# Revit family: Varmax_275_320_2-3Piquages - depuis 2013-12_FR_B
name_source: partatom
category: Equipement de génie climatique
revit_build: Autodesk Revit 2015 (Build: 20140606_1530(x64)
units: mm (PartAtom-declared; Revit-internal decimal feet)

## types (2) — shared parameters
Classe Nox = 6
Fabricant = Atlantic
Famille = Chaudière collective sol gaz
Fréquence = 50 Hz
Garantie autres pièces = 2 ans
Garantie corps de chauffe = 3 ans
Hauteur = 1877 mm  [stored 6.15814 ft]
Hauteur chaudière (hors pieds) = 1877 mm  [stored 6.15814 ft]
Hauteur de pieds mini = 45 mm
Hauteur entrée d’air (hors pieds) = 1256 mm
Hauteur piquage départ (hors pieds) = 1661 mm  [stored 5.44948 ft]
Hauteur piquage gaz (hors pieds) = 1413 mm
Hauteur piquage retour chaud (hors pieds) = 1265 mm
Largeur = 812 mm  [stored 2.66404 ft]
Largeur chaudière = 779 mm  [stored 2.55577 ft]
Largeur chaudière avec jaquette = 812 mm  [stored 2.66404 ft]
Lien données RT (Edibatec) = http://www.edibatec.org
Lien page produit = http://www.atlantic-guillot.fr
Lien pièces détachées = http://atlantic.plateforme-services.com
Longueur piquages départ / retour = 148 mm
Marque commerciale = Oui
Marque3D = Oui
Matériau corps de chauffe = Acier inoxydable
Modèle = Varmax 275
Nombre piquages = 3
Poids à vide = 502 kg
Pression d'alimentation gaz naturel = 20 ou 300 mbar
Pression d'alimentation propane = 37 mbar
Pression de service = 6 bar
Profondeur = 1341 mm  [stored 4.39961 ft]
Profondeur chaudière = 1341 mm  [stored 4.39961 ft]
Raccordement fumées = Cheminée (B23/B23p) / Ventouse (C13/C33/C53)
Réseau (mono/tri) = Monophasé
Taux de modulation = 0.2
Tension d'alimentation = 230 V
Type d'énergie = Gaz naturel ou Propane
URL = www.atlantic-guillot.fr
température de consigne départ maximale = 85 °C
volume en eau = 239 l
Ø nominal 1er retour froid = 80 mm  [stored 0.262467 ft]
Ø nominal 2eme retour chaud = 80 mm  [stored 0.262467 ft]
Ø nominal départ = 80 mm  [stored 0.262467 ft]
Ø nominal piquage gaz = 60 mm  [stored 0.19685 ft]
Ø nominal vidange condensateur = 25 mm  [stored 0.082021 ft]
Ø nominal vidange échangeur = 25 mm  [stored 0.082021 ft]
Ø piquage soupape = 32 mm  [stored 0.104987 ft]
Ø évacuation condensats = 25 mm  [stored 0.082021 ft]
Ø_Entrée d'air = 180 mm  [stored 0.590551 ft]
Ø_Sortie fumées = 180 mm  [stored 0.590551 ft]

## per-type parameters (varying)
| type | Code article | Description | Puissance utile nominale à régime 50/30 °C | Puissance utile nominale à régime 80/60 °C | Puissance électrique absorbée à Qn |
| VARMAX 275 20MB 2-3 PIQUAGES | 541518 | Chaudière sol gaz à condensation en inox 275 kW 2/3 piquages | 290 kW | 268 kW | 238 VA |
| VARMAX 320 20MB 2-3 PIQUAGES | 541522 | Chaudière sol gaz à condensation en inox 320 kW 2/3 piquages | 338 kW | 312 kW | 352 VA |

note: column(s) folded — value = type name in every type: Référence

note: [stored X ft] marks values corroborated as IEEE doubles in the binary element streams (Revit-internal decimal feet)

## geometry (parser evidence)
native form markers: Sweep x2
no freeform markers — native parametric forms only
